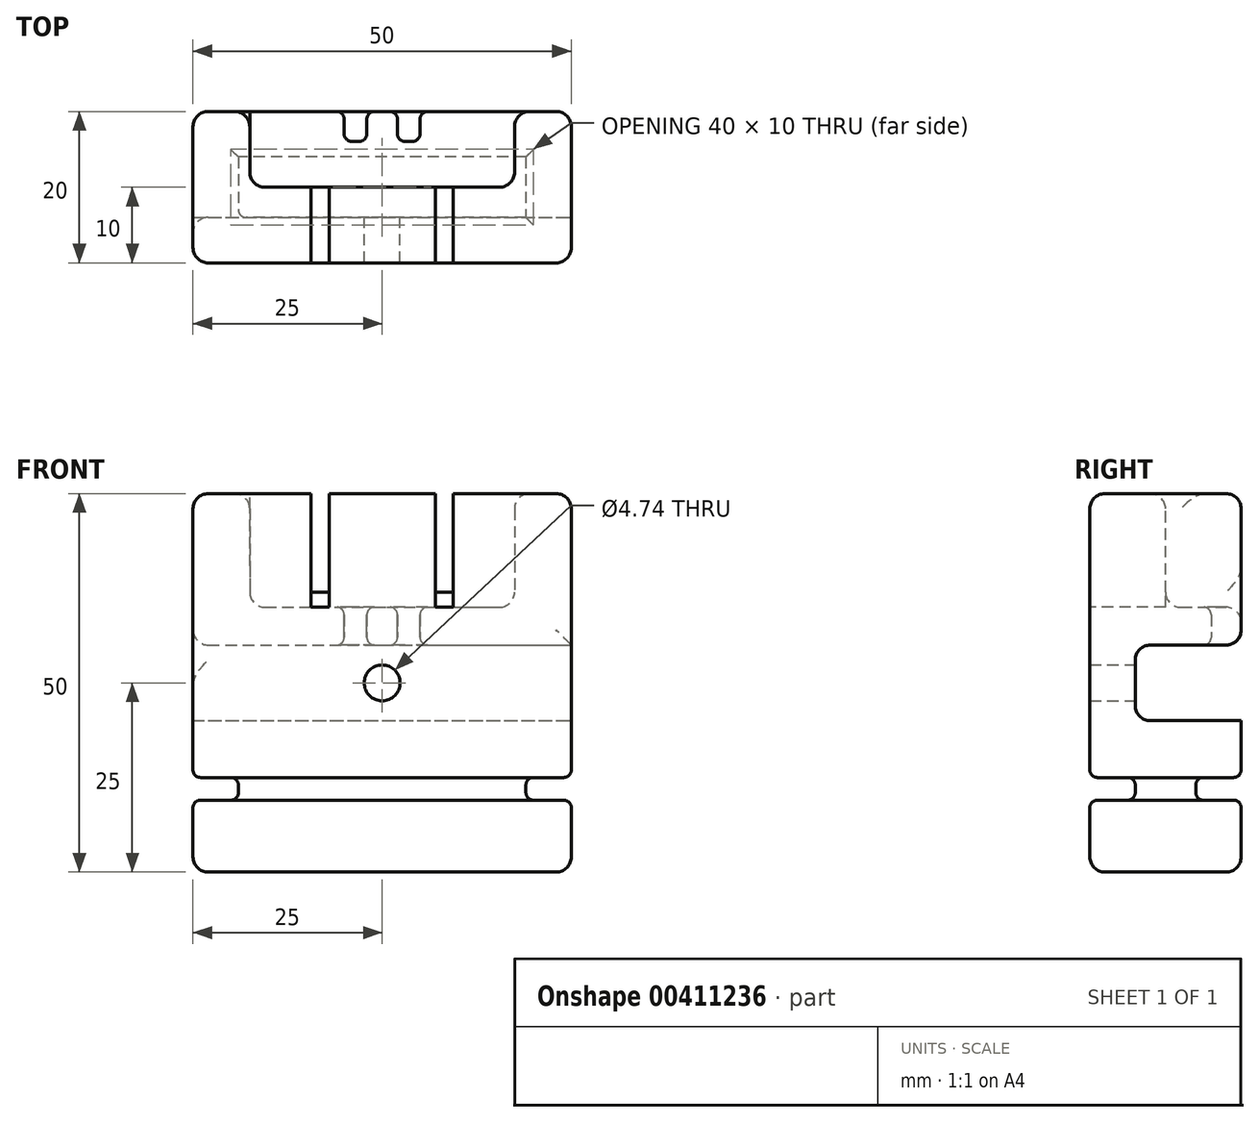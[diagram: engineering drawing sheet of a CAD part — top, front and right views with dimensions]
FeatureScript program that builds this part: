
annotation { "Feature Type Name" : "Feature", "Feature Type Description" : "" }
export const myFeature = defineFeature(function(context is Context, id is Id, definition is map)
    precondition{}
    {
        {
            var Q0;
            Q0=qCreatedBy(makeId("Front.planeOp"),FACE);
            var sketch = newSketch(context, id + "F0", { "sketchPlane" : qUnion([Q0])});
            skLineSegment(sketch, "E0.bottom", {"start": v(-25, 25) * mm, "end": v(25, 25) * mm});
            skLineSegment(sketch, "E0.top", {"start": v(-25, -25) * mm, "end": v(25, -25) * mm});
            skLineSegment(sketch, "E0.left", {"start": v(-25, 25) * mm, "end": v(-25, -25) * mm});
            skLineSegment(sketch, "E0.right", {"start": v(25, 25) * mm, "end": v(25, -25) * mm});
            skSolve(sketch);
        }
        {
            var Q0;
            Q0=makeQuery(id+"F0.imprint","IMPRINT",FACE,{"disambiguationData":[TD([[makeQuery(id+"F0.imprint","IMPRINT",EDGE,{"derivedFrom":sQuery(id+"F0.wireOp",EDGE,"E0.bottom")}),-1.0]])]});
            extrude(context, id + "F1", {"entities" : qUnion([Q0]), "endBound" : BoundingType.SYMMETRIC, "depth" : 20 * mm});
        }
        {
            var Q0;
            Q0=makeQuery(id+"F1.opExtrude","SWEPT_FACE",FACE,{"disambiguationData":[OSD([sQuery(id+"F0.wireOp",EDGE,"E0.right")])]});
            var sketch = newSketch(context, id + "F2", { "sketchPlane" : qUnion([Q0])});
            skLineSegment(sketch, "E1.bottom", {"start": v(-4, 5) * mm, "end": v(10, 5) * mm});
            skLineSegment(sketch, "E1.top", {"start": v(-4, -5) * mm, "end": v(10, -5) * mm});
            skLineSegment(sketch, "E1.left", {"start": v(-4, 5) * mm, "end": v(-4, -5) * mm});
            skLineSegment(sketch, "E1.right", {"start": v(10, 5) * mm, "end": v(10, -5) * mm});
            skSolve(sketch);
        }
        {
            var Q0;
            Q0=makeQuery(id+"F2.imprint","IMPRINT",FACE,{"disambiguationData":[TD([[makeQuery(id+"F2.imprint","IMPRINT",EDGE,{"derivedFrom":sQuery(id+"F2.wireOp",EDGE,"E1.bottom")}),-1.0]])]});
            extrude(context, id + "F3", {"entities" : qUnion([Q0]), "operationType" : NewBodyOperationType.REMOVE, "oppositeDirection" : true, "depth" : 76.7 * mm});
        }
        {
            var Q0;
            Q0=makeQuery(id+"F1.opExtrude","CAP_EDGE",EDGE,{"disambiguationData":[OSD([sQuery(id+"F0.wireOp",EDGE,"E0.bottom")])],"isStart":true});
            var Q1;
            Q1=makeQuery(id+"F3.boolean.opBoolean","COPY",EDGE,{"derivedFrom":makeQuery(id+"F3.opExtrude","SWEPT_EDGE",EDGE,{"disambiguationData":[OSD([sQuery(id+"F2.wireOp",EDGE,"E1.top"),sQuery(id+"F2.wireOp",EDGE,"E1.left")])]})});
            var Q2;
            Q2=makeQuery(id+"F3.boolean.opBoolean","COPY",EDGE,{"derivedFrom":makeQuery(id+"F3.opExtrude","SWEPT_EDGE",EDGE,{"disambiguationData":[OSD([sQuery(id+"F2.wireOp",EDGE,"E1.bottom"),sQuery(id+"F2.wireOp",EDGE,"E1.left")])]})});
            var Q3;
            Q3=makeQuery(id+"F1.opExtrude","CAP_EDGE",EDGE,{"disambiguationData":[OSD([sQuery(id+"F0.wireOp",EDGE,"E0.bottom")])],"isStart":false});
            var Q4;
            Q4=makeQuery(id+"F3.boolean.opBoolean","COPY",EDGE,{"derivedFrom":makeQuery(id+"F3.opExtrude","SWEPT_EDGE",EDGE,{"disambiguationData":[OSD([sQuery(id+"F0.wireOp",EDGE,"E0.right"),sQuery(id+"F2.wireOp",EDGE,"E1.top"),sQuery(id+"F2.wireOp",EDGE,"E1.right")])]})});
            var Q5;
            Q5=makeQuery(id+"F1.opExtrude","CAP_EDGE",EDGE,{"disambiguationData":[OSD([sQuery(id+"F0.wireOp",EDGE,"E0.top")])],"isStart":true});
            var Q6;
            Q6=makeQuery(id+"F1.opExtrude","CAP_EDGE",EDGE,{"disambiguationData":[OSD([sQuery(id+"F0.wireOp",EDGE,"E0.top")])],"isStart":false});
            var Q7;
            Q7=makeQuery(id+"F1.opExtrude","CAP_EDGE",EDGE,{"disambiguationData":[OSD([sQuery(id+"F0.wireOp",EDGE,"E0.right")])],"isStart":false});
            var Q8;
            {var subQ0=sQuery(id+"F0.wireOp",EDGE,"E0.right");var subQ1=sQuery(id+"F0.wireOp",EDGE,"E0.top");Q8=makeQuery(id+"F3.boolean.opBoolean","SPLIT",EDGE,{"disambiguationData":[TD([makeQuery(id+"F1.opExtrude","SWEPT_FACE",FACE,{"disambiguationData":[OSD([subQ1])]})])],"derivedFrom":makeQuery(id+"F1.opExtrude","CAP_EDGE",EDGE,{"disambiguationData":[OSD([subQ0])],"isStart":true})});}
            var Q9;
            {var subQ0=sQuery(id+"F0.wireOp",EDGE,"E0.left");var subQ1=sQuery(id+"F0.wireOp",EDGE,"E0.top");Q9=makeQuery(id+"F3.boolean.opBoolean","SPLIT",EDGE,{"disambiguationData":[TD([makeQuery(id+"F1.opExtrude","SWEPT_FACE",FACE,{"disambiguationData":[OSD([subQ1])]})])],"derivedFrom":makeQuery(id+"F1.opExtrude","CAP_EDGE",EDGE,{"disambiguationData":[OSD([subQ0])],"isStart":true})});}
            var Q10;
            Q10=makeQuery(id+"F1.opExtrude","CAP_EDGE",EDGE,{"disambiguationData":[OSD([sQuery(id+"F0.wireOp",EDGE,"E0.left")])],"isStart":false});
            var Q11;
            {var subQ0=sQuery(id+"F0.wireOp",EDGE,"E0.bottom");var subQ1=sQuery(id+"F0.wireOp",EDGE,"E0.left");Q11=makeQuery(id+"F3.boolean.opBoolean","SPLIT",EDGE,{"disambiguationData":[TD([makeQuery(id+"F1.opExtrude","SWEPT_FACE",FACE,{"disambiguationData":[OSD([subQ0])]})])],"derivedFrom":makeQuery(id+"F1.opExtrude","CAP_EDGE",EDGE,{"disambiguationData":[OSD([subQ1])],"isStart":true})});}
            var Q12;
            Q12=makeQuery(id+"F1.opExtrude","SWEPT_EDGE",EDGE,{"disambiguationData":[OSD([sQuery(id+"F0.wireOp",EDGE,"E0.bottom"),sQuery(id+"F0.wireOp",EDGE,"E0.left")])]});
            var Q13;
            Q13=makeQuery(id+"F1.opExtrude","SWEPT_EDGE",EDGE,{"disambiguationData":[OSD([sQuery(id+"F0.wireOp",EDGE,"E0.bottom"),sQuery(id+"F0.wireOp",EDGE,"E0.right")])]});
            var Q14;
            {var subQ0=sQuery(id+"F0.wireOp",EDGE,"E0.bottom");var subQ1=sQuery(id+"F0.wireOp",EDGE,"E0.right");Q14=makeQuery(id+"F3.boolean.opBoolean","SPLIT",EDGE,{"disambiguationData":[TD([makeQuery(id+"F1.opExtrude","SWEPT_FACE",FACE,{"disambiguationData":[OSD([subQ0])]})])],"derivedFrom":makeQuery(id+"F1.opExtrude","CAP_EDGE",EDGE,{"disambiguationData":[OSD([subQ1])],"isStart":true})});}
            var Q15;
            Q15=makeQuery(id+"F3.boolean.opBoolean","COPY",EDGE,{"derivedFrom":makeQuery(id+"F3.opExtrude","CAP_EDGE",EDGE,{"disambiguationData":[OSD([sQuery(id+"F2.wireOp",EDGE,"E1.top")])],"isStart":true})});
            var Q16;
            Q16=makeQuery(id+"F3.boolean.opBoolean","COPY",EDGE,{"derivedFrom":makeQuery(id+"F3.opExtrude","SWEPT_EDGE",EDGE,{"disambiguationData":[OSD([sQuery(id+"F0.wireOp",EDGE,"E0.right"),sQuery(id+"F2.wireOp",EDGE,"E1.bottom"),sQuery(id+"F2.wireOp",EDGE,"E1.right")])]})});
            var Q17;
            Q17=makeQuery(id+"F3.boolean.opBoolean","INTERSECT",EDGE,{"derivedFrom":[makeQuery(id+"F1.opExtrude","SWEPT_FACE",FACE,{"disambiguationData":[OSD([sQuery(id+"F0.wireOp",EDGE,"E0.left")])]}),makeQuery(id+"F3.opExtrude","SWEPT_FACE",FACE,{"disambiguationData":[OSD([sQuery(id+"F2.wireOp",EDGE,"E1.bottom")])]})]});
            var Q18;
            Q18=makeQuery(id+"F1.opExtrude","SWEPT_EDGE",EDGE,{"disambiguationData":[OSD([sQuery(id+"F0.wireOp",EDGE,"E0.top"),sQuery(id+"F0.wireOp",EDGE,"E0.left")])]});
            var Q19;
            Q19=makeQuery(id+"F1.opExtrude","SWEPT_EDGE",EDGE,{"disambiguationData":[OSD([sQuery(id+"F0.wireOp",EDGE,"E0.top"),sQuery(id+"F0.wireOp",EDGE,"E0.right")])]});
            fillet(context, id + "F4", {"entities" : qUnion([Q0, Q1, Q2, Q3, Q4, Q5, Q6, Q7, Q8, Q9, Q10, Q11, Q12, Q13, Q14, Q15, Q16, Q17, Q18, Q19]), "radius" : 2 * mm, "tangentPropagation" : true, "allowEdgeOverflow" : false});
        }
        {
            var Q0;
            Q0=qCreatedBy(makeId("Right.planeOp"),FACE);
            var sketch = newSketch(context, id + "F5", { "sketchPlane" : qUnion([Q0])});
            skLineSegment(sketch, "E2.bottom", {"start": v(0, 30) * mm, "end": v(13.71, 30) * mm});
            skLineSegment(sketch, "E2.top", {"start": v(0, 10) * mm, "end": v(13.71, 10) * mm});
            skLineSegment(sketch, "E2.left", {"start": v(0, 30) * mm, "end": v(0, 10) * mm});
            skLineSegment(sketch, "E2.right", {"start": v(13.71, 30) * mm, "end": v(13.71, 10) * mm});
            skSolve(sketch);
        }
        {
            var Q0;
            Q0=makeQuery(id+"F5.imprint","IMPRINT",FACE,{"disambiguationData":[TD([[makeQuery(id+"F5.imprint","IMPRINT",EDGE,{"derivedFrom":sQuery(id+"F5.wireOp",EDGE,"E2.bottom")}),-1.0]])]});
            extrude(context, id + "F6", {"entities" : qUnion([Q0]), "operationType" : NewBodyOperationType.REMOVE, "endBound" : BoundingType.SYMMETRIC, "oppositeDirection" : true, "depth" : 35 * mm});
        }
        {
            var Q0;
            Q0=makeQuery(id+"F6.boolean.opBoolean","COPY",EDGE,{"derivedFrom":makeQuery(id+"F6.opExtrude","SWEPT_EDGE",EDGE,{"disambiguationData":[OSD([sQuery(id+"F5.wireOp",EDGE,"E2.top"),sQuery(id+"F5.wireOp",EDGE,"E2.left")])]})});
            var Q1;
            Q1=makeQuery(id+"F6.boolean.opBoolean","INTERSECT",EDGE,{"derivedFrom":[makeQuery(id+"F1.opExtrude","SWEPT_FACE",FACE,{"disambiguationData":[OSD([sQuery(id+"F0.wireOp",EDGE,"E0.bottom")])]}),makeQuery(id+"F6.opExtrude","SWEPT_FACE",FACE,{"disambiguationData":[OSD([sQuery(id+"F5.wireOp",EDGE,"E2.left")])]})]});
            var Q2;
            Q2=makeQuery(id+"F6.boolean.opBoolean","INTERSECT",EDGE,{"derivedFrom":[makeQuery(id+"F1.opExtrude","SWEPT_FACE",FACE,{"disambiguationData":[OSD([sQuery(id+"F0.wireOp",EDGE,"E0.bottom")])]}),makeQuery(id+"F6.opExtrude","CAP_FACE",FACE,{"disambiguationData":[OSD([sQuery(id+"F5.wireOp",EDGE,"E2.bottom"),sQuery(id+"F5.wireOp",EDGE,"E2.top"),sQuery(id+"F5.wireOp",EDGE,"E2.left"),sQuery(id+"F5.wireOp",EDGE,"E2.right")])],"isStart":true})]});
            var Q3;
            Q3=makeQuery(id+"F6.boolean.opBoolean","COPY",EDGE,{"derivedFrom":makeQuery(id+"F6.opExtrude","CAP_EDGE",EDGE,{"disambiguationData":[OSD([sQuery(id+"F5.wireOp",EDGE,"E2.top")])],"isStart":true})});
            var Q4;
            {var subQ0=sQuery(id+"F0.wireOp",EDGE,"E0.bottom");var subQ1=sQuery(id+"F0.wireOp",EDGE,"E0.left");var subQ2=sQuery(id+"F0.wireOp",EDGE,"E0.right");Q4=makeQuery(id+"F6.boolean.opBoolean","INTERSECT",EDGE,{"derivedFrom":[makeQuery(id+"F3.boolean.opBoolean","SPLIT",FACE,{"disambiguationData":[TD([makeQuery(id+"F1.opExtrude","SWEPT_FACE",FACE,{"disambiguationData":[OSD([subQ0])]})])],"derivedFrom":makeQuery(id+"F1.opExtrude","CAP_FACE",FACE,{"disambiguationData":[OSD([subQ0,sQuery(id+"F0.wireOp",EDGE,"E0.top"),subQ1,subQ2])],"isStart":true})}),makeQuery(id+"F6.opExtrude","SWEPT_FACE",FACE,{"disambiguationData":[OSD([sQuery(id+"F5.wireOp",EDGE,"E2.top")])]})]});}
            var Q5;
            Q5=makeQuery(id+"F6.boolean.opBoolean","COPY",EDGE,{"derivedFrom":makeQuery(id+"F6.opExtrude","CAP_EDGE",EDGE,{"disambiguationData":[OSD([sQuery(id+"F5.wireOp",EDGE,"E2.top")])],"isStart":false})});
            var Q6;
            Q6=makeQuery(id+"F6.boolean.opBoolean","COPY",EDGE,{"derivedFrom":makeQuery(id+"F6.opExtrude","CAP_EDGE",EDGE,{"disambiguationData":[OSD([sQuery(id+"F5.wireOp",EDGE,"E2.left")])],"isStart":false})});
            var Q7;
            Q7=makeQuery(id+"F6.boolean.opBoolean","COPY",EDGE,{"derivedFrom":makeQuery(id+"F6.opExtrude","CAP_EDGE",EDGE,{"disambiguationData":[OSD([sQuery(id+"F5.wireOp",EDGE,"E2.left")])],"isStart":true})});
            fillet(context, id + "F7", {"entities" : qUnion([Q0, Q1, Q2, Q3, Q4, Q5, Q6, Q7]), "radius" : 2 * mm, "tangentPropagation" : true, "allowEdgeOverflow" : false});
        }
        {
            var Q0;
            Q0=qCreatedBy(makeId("Top.planeOp"),FACE);
            var sketch = newSketch(context, id + "F8", { "sketchPlane" : qUnion([Q0])});
            skLineSegment(sketch, "E3.bottom", {"start": v(2.01, 11.8) * mm, "end": v(5.01, 11.8) * mm});
            skLineSegment(sketch, "E3.top", {"start": v(2.01, 6.04) * mm, "end": v(5.01, 6.04) * mm});
            skLineSegment(sketch, "E3.left", {"start": v(2.01, 11.8) * mm, "end": v(2.01, 6.04) * mm});
            skLineSegment(sketch, "E3.right", {"start": v(5.01, 11.8) * mm, "end": v(5.01, 6.04) * mm});
            skLineSegment(sketch, "E4.MirrorCS", {"start": v(-2.01, 6.04) * mm, "end": v(-5.01, 6.04) * mm});
            skLineSegment(sketch, "E5.MirrorCS", {"start": v(-5.01, 11.8) * mm, "end": v(-5.01, 6.04) * mm});
            skLineSegment(sketch, "E6.MirrorCS", {"start": v(-2.01, 11.8) * mm, "end": v(-5.01, 11.8) * mm});
            skLineSegment(sketch, "E7.MirrorCS", {"start": v(-2.01, 11.8) * mm, "end": v(-2.01, 6.04) * mm});
            skSolve(sketch);
        }
        {
            var Q0;
            Q0=makeQuery(id+"F8.imprint","IMPRINT",FACE,{"disambiguationData":[TD([[makeQuery(id+"F8.imprint","IMPRINT",EDGE,{"derivedFrom":sQuery(id+"F8.wireOp",EDGE,"E3.bottom")}),-1.0]])]});
            var Q1;
            Q1=makeQuery(id+"F8.imprint","IMPRINT",FACE,{"disambiguationData":[TD([[makeQuery(id+"F8.imprint","IMPRINT",EDGE,{"derivedFrom":sQuery(id+"F8.wireOp",EDGE,"E4.MirrorCS")}),-1.0]])]});
            extrude(context, id + "F9", {"entities" : qUnion([Q0, Q1]), "operationType" : NewBodyOperationType.REMOVE, "depth" : 29.72 * mm});
        }
        {
            var Q0;
            Q0=makeQuery(id+"F9.boolean.opBoolean","INTERSECT",EDGE,{"derivedFrom":[makeQuery(id+"F6.boolean.opBoolean","COPY",FACE,{"derivedFrom":makeQuery(id+"F6.opExtrude","SWEPT_FACE",FACE,{"disambiguationData":[OSD([sQuery(id+"F5.wireOp",EDGE,"E2.top")])]})}),makeQuery(id+"F9.opExtrude","SWEPT_FACE",FACE,{"disambiguationData":[OSD([sQuery(id+"F8.wireOp",EDGE,"E3.top")])]})]});
            var Q1;
            Q1=makeQuery(id+"F9.boolean.opBoolean","COPY",EDGE,{"derivedFrom":makeQuery(id+"F9.opExtrude","SWEPT_EDGE",EDGE,{"disambiguationData":[OSD([sQuery(id+"F8.wireOp",EDGE,"E3.top"),sQuery(id+"F8.wireOp",EDGE,"E3.left")])]})});
            var Q2;
            Q2=makeQuery(id+"F9.boolean.opBoolean","INTERSECT",EDGE,{"derivedFrom":[makeQuery(id+"F6.boolean.opBoolean","COPY",FACE,{"derivedFrom":makeQuery(id+"F6.opExtrude","SWEPT_FACE",FACE,{"disambiguationData":[OSD([sQuery(id+"F5.wireOp",EDGE,"E2.top")])]})}),makeQuery(id+"F9.opExtrude","SWEPT_FACE",FACE,{"disambiguationData":[OSD([sQuery(id+"F8.wireOp",EDGE,"E3.left")])]})]});
            var Q3;
            Q3=makeQuery(id+"F9.boolean.opBoolean","INTERSECT",EDGE,{"derivedFrom":[makeQuery(id+"F6.boolean.opBoolean","COPY",FACE,{"derivedFrom":makeQuery(id+"F6.opExtrude","SWEPT_FACE",FACE,{"disambiguationData":[OSD([sQuery(id+"F5.wireOp",EDGE,"E2.top")])]})}),makeQuery(id+"F9.opExtrude","SWEPT_FACE",FACE,{"disambiguationData":[OSD([sQuery(id+"F8.wireOp",EDGE,"E4.MirrorCS")])]})]});
            var Q4;
            Q4=makeQuery(id+"F9.boolean.opBoolean","INTERSECT",EDGE,{"derivedFrom":[makeQuery(id+"F6.boolean.opBoolean","COPY",FACE,{"derivedFrom":makeQuery(id+"F6.opExtrude","SWEPT_FACE",FACE,{"disambiguationData":[OSD([sQuery(id+"F5.wireOp",EDGE,"E2.top")])]})}),makeQuery(id+"F9.opExtrude","SWEPT_FACE",FACE,{"disambiguationData":[OSD([sQuery(id+"F8.wireOp",EDGE,"E5.MirrorCS")])]})]});
            var Q5;
            Q5=makeQuery(id+"F9.boolean.opBoolean","INTERSECT",EDGE,{"derivedFrom":[makeQuery(id+"F3.boolean.opBoolean","COPY",FACE,{"derivedFrom":makeQuery(id+"F3.opExtrude","SWEPT_FACE",FACE,{"disambiguationData":[OSD([sQuery(id+"F2.wireOp",EDGE,"E1.bottom")])]})}),makeQuery(id+"F9.opExtrude","SWEPT_FACE",FACE,{"disambiguationData":[OSD([sQuery(id+"F8.wireOp",EDGE,"E3.top")])]})]});
            var Q6;
            Q6=makeQuery(id+"F9.boolean.opBoolean","COPY",EDGE,{"derivedFrom":makeQuery(id+"F9.opExtrude","SWEPT_EDGE",EDGE,{"disambiguationData":[OSD([sQuery(id+"F8.wireOp",EDGE,"E3.top"),sQuery(id+"F8.wireOp",EDGE,"E3.right")])]})});
            var Q7;
            {var subQ0=sQuery(id+"F2.wireOp",EDGE,"E1.right");var subQ1=sQuery(id+"F2.wireOp",EDGE,"E1.bottom");var subQ2=sQuery(id+"F0.wireOp",EDGE,"E0.right");Q7=makeQuery(id+"F9.boolean.opBoolean","INTERSECT",EDGE,{"derivedFrom":[makeQuery(id+"F4.opFillet","BLEND_FACE",FACE,{"disambiguationData":[OSD([subQ2,subQ1,subQ0]),TDD([makeQuery(id+"F3.boolean.opBoolean","COPY",EDGE,{"derivedFrom":makeQuery(id+"F3.opExtrude","SWEPT_EDGE",EDGE,{"disambiguationData":[OSD([subQ2,subQ1,subQ0])]})})])]}),makeQuery(id+"F9.opExtrude","SWEPT_FACE",FACE,{"disambiguationData":[OSD([sQuery(id+"F8.wireOp",EDGE,"E3.right")])]})]});}
            var Q8;
            Q8=makeQuery(id+"F9.boolean.opBoolean","INTERSECT",EDGE,{"derivedFrom":[makeQuery(id+"F3.boolean.opBoolean","COPY",FACE,{"derivedFrom":makeQuery(id+"F3.opExtrude","SWEPT_FACE",FACE,{"disambiguationData":[OSD([sQuery(id+"F2.wireOp",EDGE,"E1.bottom")])]})}),makeQuery(id+"F9.opExtrude","SWEPT_FACE",FACE,{"disambiguationData":[OSD([sQuery(id+"F8.wireOp",EDGE,"E7.MirrorCS")])]})]});
            var Q9;
            Q9=makeQuery(id+"F9.boolean.opBoolean","INTERSECT",EDGE,{"derivedFrom":[makeQuery(id+"F3.boolean.opBoolean","COPY",FACE,{"derivedFrom":makeQuery(id+"F3.opExtrude","SWEPT_FACE",FACE,{"disambiguationData":[OSD([sQuery(id+"F2.wireOp",EDGE,"E1.bottom")])]})}),makeQuery(id+"F9.opExtrude","SWEPT_FACE",FACE,{"disambiguationData":[OSD([sQuery(id+"F8.wireOp",EDGE,"E4.MirrorCS")])]})]});
            var Q10;
            Q10=makeQuery(id+"F9.boolean.opBoolean","COPY",EDGE,{"derivedFrom":makeQuery(id+"F9.opExtrude","SWEPT_EDGE",EDGE,{"disambiguationData":[OSD([sQuery(id+"F8.wireOp",EDGE,"E4.MirrorCS"),sQuery(id+"F8.wireOp",EDGE,"E7.MirrorCS")])]})});
            var Q11;
            Q11=makeQuery(id+"F9.boolean.opBoolean","COPY",EDGE,{"derivedFrom":makeQuery(id+"F9.opExtrude","SWEPT_EDGE",EDGE,{"disambiguationData":[OSD([sQuery(id+"F8.wireOp",EDGE,"E4.MirrorCS"),sQuery(id+"F8.wireOp",EDGE,"E5.MirrorCS")])]})});
            fillet(context, id + "F10", {"entities" : qUnion([Q0, Q1, Q2, Q3, Q4, Q5, Q6, Q7, Q8, Q9, Q10, Q11]), "radius" : 1 * mm, "tangentPropagation" : true, "allowEdgeOverflow" : false});
        }
        {
            var Q0;
            {var subQ0=sQuery(id+"F0.wireOp",EDGE,"E0.top");var subQ1=sQuery(id+"F0.wireOp",EDGE,"E0.left");var subQ2=sQuery(id+"F0.wireOp",EDGE,"E0.right");Q0=makeQuery(id+"F3.boolean.opBoolean","SPLIT",FACE,{"disambiguationData":[TD([makeQuery(id+"F1.opExtrude","SWEPT_FACE",FACE,{"disambiguationData":[OSD([subQ0])]})])],"derivedFrom":makeQuery(id+"F1.opExtrude","CAP_FACE",FACE,{"disambiguationData":[OSD([sQuery(id+"F0.wireOp",EDGE,"E0.bottom"),subQ0,subQ1,subQ2])],"isStart":true})});}
            var sketch = newSketch(context, id + "F11", { "sketchPlane" : qUnion([Q0])});
            skLineSegment(sketch, "E8.bottom", {"start": v(-25, -12.5) * mm, "end": v(25, -12.5) * mm});
            skLineSegment(sketch, "E8.top", {"start": v(-25, -15.5) * mm, "end": v(25, -15.5) * mm});
            skLineSegment(sketch, "E8.left", {"start": v(-25, -12.5) * mm, "end": v(-25, -15.5) * mm});
            skLineSegment(sketch, "E8.right", {"start": v(25, -12.5) * mm, "end": v(25, -15.5) * mm});
            skSolve(sketch);
        }
        {
            var Q0;
            {var subQ0=sQuery(id+"F11.wireOp",EDGE,"E8.bottom");var subQ1=sQuery(id+"F0.wireOp",EDGE,"E0.top");var subQ2=makeQuery(id+"F1.opExtrude","SWEPT_FACE",FACE,{"disambiguationData":[OSD([subQ1])]});var subQ3=sQuery(id+"F0.wireOp",EDGE,"E0.left");var subQ5=sQuery(id+"F0.wireOp",EDGE,"E0.right");var subQ8=makeQuery(id+"F1.opExtrude","CAP_FACE",FACE,{"disambiguationData":[OSD([sQuery(id+"F0.wireOp",EDGE,"E0.bottom"),subQ1,subQ3,subQ5])],"isStart":true});var subQ9=makeQuery(id+"F3.boolean.opBoolean","SPLIT",FACE,{"disambiguationData":[TD([subQ2])],"derivedFrom":subQ8});var subQ10=makeQuery(id+"F4.opFillet","BLEND_EDGE",EDGE,{"blendedFrom":[makeQuery(id+"F3.boolean.opBoolean","SPLIT",EDGE,{"disambiguationData":[TD([subQ2])],"derivedFrom":makeQuery(id+"F1.opExtrude","CAP_EDGE",EDGE,{"disambiguationData":[OSD([subQ5])],"isStart":true})}),subQ9],"blendedInto":[subQ9]});var subQ11=makeQuery(id+"F11.imprint","INTERSECT",VERTEX,{"derivedFrom":[subQ10,subQ0]});Q0=makeQuery(id+"F11.imprint","IMPRINT",FACE,{"disambiguationData":[TD([[makeQuery(id+"F11.imprint","IMPRINT",EDGE,{"disambiguationData":[TD([[subQ11,-1.0]])],"derivedFrom":subQ0}),-1.0]])]});}
            var Q1;
            {var subQ0=sQuery(id+"F11.wireOp",EDGE,"E8.left");Q1=makeQuery(id+"F11.imprint","IMPRINT",FACE,{"disambiguationData":[TD([[makeQuery(id+"F11.imprint","IMPRINT",EDGE,{"derivedFrom":subQ0}),1.0]])]});}
            var Q2;
            {var subQ0=sQuery(id+"F11.wireOp",EDGE,"E8.right");Q2=makeQuery(id+"F11.imprint","IMPRINT",FACE,{"disambiguationData":[TD([[makeQuery(id+"F11.imprint","IMPRINT",EDGE,{"derivedFrom":subQ0}),-1.0]])]});}
            extrude(context, id + "F12", {"entities" : qUnion([Q0, Q1, Q2]), "operationType" : NewBodyOperationType.REMOVE, "oppositeDirection" : true, "depth" : 6 * mm});
        }
        {
            var Q0;
            Q0=makeQuery(id+"F1.opExtrude","SWEPT_FACE",FACE,{"disambiguationData":[OSD([sQuery(id+"F0.wireOp",EDGE,"E0.right")])]});
            var sketch = newSketch(context, id + "F13", { "sketchPlane" : qUnion([Q0])});
            skLineSegment(sketch, "E9.bottom", {"start": v(4, -15.5) * mm, "end": v(-15.57, -15.5) * mm});
            skLineSegment(sketch, "E9.top", {"start": v(4, -12.5) * mm, "end": v(-15.57, -12.5) * mm});
            skLineSegment(sketch, "E9.left", {"start": v(4, -15.5) * mm, "end": v(4, -12.5) * mm});
            skLineSegment(sketch, "E9.right", {"start": v(-15.57, -15.5) * mm, "end": v(-15.57, -12.5) * mm});
            skSolve(sketch);
        }
        {
            var Q0;
            {var subQ0=sQuery(id+"F13.wireOp",EDGE,"E9.right");Q0=makeQuery(id+"F13.imprint","IMPRINT",FACE,{"disambiguationData":[TD([[makeQuery(id+"F13.imprint","IMPRINT",EDGE,{"derivedFrom":subQ0}),-1.0]])]});}
            var Q1;
            {var subQ0=sQuery(id+"F13.wireOp",EDGE,"E9.left");Q1=makeQuery(id+"F13.imprint","IMPRINT",FACE,{"disambiguationData":[TD([[makeQuery(id+"F13.imprint","IMPRINT",EDGE,{"derivedFrom":subQ0}),-1.0]])]});}
            extrude(context, id + "F14", {"entities" : qUnion([Q0, Q1]), "operationType" : NewBodyOperationType.REMOVE, "oppositeDirection" : true, "depth" : 6 * mm});
        }
        {
            var Q0;
            Q0=makeQuery(id+"F1.opExtrude","CAP_FACE",FACE,{"disambiguationData":[OSD([sQuery(id+"F0.wireOp",EDGE,"E0.bottom"),sQuery(id+"F0.wireOp",EDGE,"E0.top"),sQuery(id+"F0.wireOp",EDGE,"E0.left"),sQuery(id+"F0.wireOp",EDGE,"E0.right")])],"isStart":false});
            var sketch = newSketch(context, id + "F15", { "sketchPlane" : qUnion([Q0])});
            skLineSegment(sketch, "E10.bottom", {"start": v(19, -15.5) * mm, "end": v(-31.6, -15.5) * mm});
            skLineSegment(sketch, "E10.top", {"start": v(19, -12.5) * mm, "end": v(-31.6, -12.5) * mm});
            skLineSegment(sketch, "E10.left", {"start": v(19, -15.5) * mm, "end": v(19, -12.5) * mm});
            skLineSegment(sketch, "E10.right", {"start": v(-31.6, -15.5) * mm, "end": v(-31.6, -12.5) * mm});
            skSolve(sketch);
        }
        {
            var Q0;
            {var subQ0=sQuery(id+"F15.wireOp",EDGE,"E10.right");Q0=makeQuery(id+"F15.imprint","IMPRINT",FACE,{"disambiguationData":[TD([[makeQuery(id+"F15.imprint","IMPRINT",EDGE,{"derivedFrom":subQ0}),-1.0]])]});}
            var Q1;
            {var subQ0=sQuery(id+"F15.wireOp",EDGE,"E10.left");Q1=makeQuery(id+"F15.imprint","IMPRINT",FACE,{"disambiguationData":[TD([[makeQuery(id+"F15.imprint","IMPRINT",EDGE,{"derivedFrom":subQ0}),1.0]])]});}
            extrude(context, id + "F16", {"entities" : qUnion([Q0, Q1]), "operationType" : NewBodyOperationType.REMOVE, "oppositeDirection" : true, "depth" : 6 * mm});
        }
        {
            var Q0;
            Q0=makeQuery(id+"F1.opExtrude","SWEPT_FACE",FACE,{"disambiguationData":[OSD([sQuery(id+"F0.wireOp",EDGE,"E0.left")])]});
            var sketch = newSketch(context, id + "F17", { "sketchPlane" : qUnion([Q0])});
            skLineSegment(sketch, "E11.bottom", {"start": v(-4, -12.5) * mm, "end": v(13.16, -12.5) * mm});
            skLineSegment(sketch, "E11.top", {"start": v(-4, -15.5) * mm, "end": v(13.16, -15.5) * mm});
            skLineSegment(sketch, "E11.left", {"start": v(-4, -12.5) * mm, "end": v(-4, -15.5) * mm});
            skLineSegment(sketch, "E11.right", {"start": v(13.16, -12.5) * mm, "end": v(13.16, -15.5) * mm});
            skSolve(sketch);
        }
        {
            var Q0;
            {var subQ0=sQuery(id+"F17.wireOp",EDGE,"E11.left");Q0=makeQuery(id+"F17.imprint","IMPRINT",FACE,{"disambiguationData":[TD([[makeQuery(id+"F17.imprint","IMPRINT",EDGE,{"derivedFrom":subQ0}),1.0]])]});}
            var Q1;
            {var subQ15=sQuery(id+"F17.wireOp",EDGE,"E11.right");Q1=makeQuery(id+"F17.imprint","IMPRINT",FACE,{"disambiguationData":[TD([[makeQuery(id+"F17.imprint","IMPRINT",EDGE,{"derivedFrom":subQ15}),-1.0]])]});}
            extrude(context, id + "F18", {"entities" : qUnion([Q0, Q1]), "operationType" : NewBodyOperationType.REMOVE, "oppositeDirection" : true, "depth" : 6 * mm});
        }
        {
            var Q0;
            Q0=makeQuery(id+"F12.boolean.opBoolean","COPY",EDGE,{"derivedFrom":makeQuery(id+"F12.opExtrude","CAP_EDGE",EDGE,{"disambiguationData":[OSD([sQuery(id+"F11.wireOp",EDGE,"E8.top")])],"isStart":true})});
            var Q1;
            Q1=makeQuery(id+"F12.boolean.opBoolean","COPY",EDGE,{"derivedFrom":makeQuery(id+"F12.opExtrude","CAP_EDGE",EDGE,{"disambiguationData":[OSD([sQuery(id+"F11.wireOp",EDGE,"E8.top")])],"isStart":false})});
            var Q2;
            Q2=makeQuery(id+"F14.boolean.opBoolean","COPY",EDGE,{"derivedFrom":makeQuery(id+"F14.opExtrude","CAP_EDGE",EDGE,{"disambiguationData":[OSD([sQuery(id+"F13.wireOp",EDGE,"E9.top")])],"isStart":false})});
            var Q3;
            Q3=makeQuery(id+"F12.boolean.opBoolean","COPY",EDGE,{"derivedFrom":makeQuery(id+"F12.opExtrude","CAP_EDGE",EDGE,{"disambiguationData":[OSD([sQuery(id+"F11.wireOp",EDGE,"E8.bottom")])],"isStart":false})});
            var Q4;
            Q4=makeQuery(id+"F12.boolean.opBoolean","COPY",EDGE,{"derivedFrom":makeQuery(id+"F12.opExtrude","CAP_EDGE",EDGE,{"disambiguationData":[OSD([sQuery(id+"F11.wireOp",EDGE,"E8.bottom")])],"isStart":true})});
            var Q5;
            {var subQ0=sQuery(id+"F0.wireOp",EDGE,"E0.right");var subQ1=sQuery(id+"F0.wireOp",EDGE,"E0.top");Q5=makeQuery(id+"F12.boolean.opBoolean","INTERSECT",EDGE,{"derivedFrom":[makeQuery(id+"F4.opFillet","BLEND_FACE",FACE,{"disambiguationData":[OSD([subQ0]),TDD([makeQuery(id+"F3.boolean.opBoolean","SPLIT",EDGE,{"disambiguationData":[TD([makeQuery(id+"F1.opExtrude","SWEPT_FACE",FACE,{"disambiguationData":[OSD([subQ1])]})])],"derivedFrom":makeQuery(id+"F1.opExtrude","CAP_EDGE",EDGE,{"disambiguationData":[OSD([subQ0])],"isStart":true})})])]}),makeQuery(id+"F12.opExtrude","SWEPT_FACE",FACE,{"disambiguationData":[OSD([sQuery(id+"F11.wireOp",EDGE,"E8.bottom")])]})]});}
            var Q6;
            Q6=makeQuery(id+"F14.boolean.opBoolean","MERGE",EDGE,{"derivedFrom":[makeQuery(id+"F12.boolean.opBoolean","COPY",EDGE,{"derivedFrom":makeQuery(id+"F12.opExtrude","SWEPT_EDGE",EDGE,{"disambiguationData":[OSD([sQuery(id+"F11.wireOp",EDGE,"E8.bottom"),sQuery(id+"F11.wireOp",EDGE,"E8.left")])]})}),makeQuery(id+"F14.opExtrude","CAP_EDGE",EDGE,{"disambiguationData":[OSD([sQuery(id+"F13.wireOp",EDGE,"E9.top")])],"isStart":true})]});
            var Q7;
            Q7=makeQuery(id+"F14.boolean.opBoolean","COPY",EDGE,{"derivedFrom":makeQuery(id+"F14.opExtrude","CAP_EDGE",EDGE,{"disambiguationData":[OSD([sQuery(id+"F13.wireOp",EDGE,"E9.left")])],"isStart":false})});
            var Q8;
            Q8=makeQuery(id+"F14.boolean.opBoolean","COPY",EDGE,{"derivedFrom":makeQuery(id+"F14.opExtrude","CAP_EDGE",EDGE,{"disambiguationData":[OSD([sQuery(id+"F13.wireOp",EDGE,"E9.bottom")])],"isStart":false})});
            var Q9;
            Q9=makeQuery(id+"F14.boolean.opBoolean","MERGE",EDGE,{"derivedFrom":[makeQuery(id+"F12.boolean.opBoolean","COPY",EDGE,{"derivedFrom":makeQuery(id+"F12.opExtrude","SWEPT_EDGE",EDGE,{"disambiguationData":[OSD([sQuery(id+"F11.wireOp",EDGE,"E8.top"),sQuery(id+"F11.wireOp",EDGE,"E8.left")])]})}),makeQuery(id+"F14.opExtrude","CAP_EDGE",EDGE,{"disambiguationData":[OSD([sQuery(id+"F13.wireOp",EDGE,"E9.bottom")])],"isStart":true})]});
            var Q10;
            {var subQ0=sQuery(id+"F0.wireOp",EDGE,"E0.right");var subQ1=sQuery(id+"F0.wireOp",EDGE,"E0.top");Q10=makeQuery(id+"F12.boolean.opBoolean","INTERSECT",EDGE,{"derivedFrom":[makeQuery(id+"F4.opFillet","BLEND_FACE",FACE,{"disambiguationData":[OSD([subQ0]),TDD([makeQuery(id+"F3.boolean.opBoolean","SPLIT",EDGE,{"disambiguationData":[TD([makeQuery(id+"F1.opExtrude","SWEPT_FACE",FACE,{"disambiguationData":[OSD([subQ1])]})])],"derivedFrom":makeQuery(id+"F1.opExtrude","CAP_EDGE",EDGE,{"disambiguationData":[OSD([subQ0])],"isStart":true})})])]}),makeQuery(id+"F12.opExtrude","SWEPT_FACE",FACE,{"disambiguationData":[OSD([sQuery(id+"F11.wireOp",EDGE,"E8.top")])]})]});}
            var Q11;
            {var subQ0=sQuery(id+"F0.wireOp",EDGE,"E0.right");Q11=makeQuery(id+"F14.boolean.opBoolean","INTERSECT",EDGE,{"derivedFrom":[makeQuery(id+"F4.opFillet","BLEND_FACE",FACE,{"disambiguationData":[OSD([subQ0]),TDD([makeQuery(id+"F1.opExtrude","CAP_EDGE",EDGE,{"disambiguationData":[OSD([subQ0])],"isStart":false})])]}),makeQuery(id+"F14.opExtrude","SWEPT_FACE",FACE,{"disambiguationData":[OSD([sQuery(id+"F13.wireOp",EDGE,"E9.bottom")])]})]});}
            var Q12;
            Q12=makeQuery(id+"F16.boolean.opBoolean","COPY",EDGE,{"derivedFrom":makeQuery(id+"F16.opExtrude","CAP_EDGE",EDGE,{"disambiguationData":[OSD([sQuery(id+"F15.wireOp",EDGE,"E10.bottom")])],"isStart":false})});
            var Q13;
            Q13=makeQuery(id+"F16.boolean.opBoolean","MERGE",EDGE,{"derivedFrom":[makeQuery(id+"F14.boolean.opBoolean","INTERSECT",EDGE,{"derivedFrom":[makeQuery(id+"F1.opExtrude","CAP_FACE",FACE,{"disambiguationData":[OSD([sQuery(id+"F0.wireOp",EDGE,"E0.bottom"),sQuery(id+"F0.wireOp",EDGE,"E0.top"),sQuery(id+"F0.wireOp",EDGE,"E0.left"),sQuery(id+"F0.wireOp",EDGE,"E0.right")])],"isStart":false}),makeQuery(id+"F14.opExtrude","SWEPT_FACE",FACE,{"disambiguationData":[OSD([sQuery(id+"F13.wireOp",EDGE,"E9.bottom")])]})]}),makeQuery(id+"F16.opExtrude","CAP_EDGE",EDGE,{"disambiguationData":[OSD([sQuery(id+"F15.wireOp",EDGE,"E10.bottom")])],"isStart":true})]});
            var Q14;
            Q14=makeQuery(id+"F16.boolean.opBoolean","COPY",EDGE,{"derivedFrom":makeQuery(id+"F16.opExtrude","CAP_EDGE",EDGE,{"disambiguationData":[OSD([sQuery(id+"F15.wireOp",EDGE,"E10.top")])],"isStart":false})});
            var Q15;
            Q15=makeQuery(id+"F16.boolean.opBoolean","MERGE",EDGE,{"derivedFrom":[makeQuery(id+"F14.boolean.opBoolean","INTERSECT",EDGE,{"derivedFrom":[makeQuery(id+"F1.opExtrude","CAP_FACE",FACE,{"disambiguationData":[OSD([sQuery(id+"F0.wireOp",EDGE,"E0.bottom"),sQuery(id+"F0.wireOp",EDGE,"E0.top"),sQuery(id+"F0.wireOp",EDGE,"E0.left"),sQuery(id+"F0.wireOp",EDGE,"E0.right")])],"isStart":false}),makeQuery(id+"F14.opExtrude","SWEPT_FACE",FACE,{"disambiguationData":[OSD([sQuery(id+"F13.wireOp",EDGE,"E9.top")])]})]}),makeQuery(id+"F16.opExtrude","CAP_EDGE",EDGE,{"disambiguationData":[OSD([sQuery(id+"F15.wireOp",EDGE,"E10.top")])],"isStart":true})]});
            var Q16;
            Q16=makeQuery(id+"F18.boolean.opBoolean","COPY",EDGE,{"derivedFrom":makeQuery(id+"F18.opExtrude","CAP_EDGE",EDGE,{"disambiguationData":[OSD([sQuery(id+"F17.wireOp",EDGE,"E11.bottom")])],"isStart":false})});
            var Q17;
            Q17=makeQuery(id+"F18.boolean.opBoolean","MERGE",EDGE,{"derivedFrom":[makeQuery(id+"F12.boolean.opBoolean","COPY",EDGE,{"derivedFrom":makeQuery(id+"F12.opExtrude","SWEPT_EDGE",EDGE,{"disambiguationData":[OSD([sQuery(id+"F11.wireOp",EDGE,"E8.bottom"),sQuery(id+"F11.wireOp",EDGE,"E8.right")])]})}),makeQuery(id+"F16.boolean.opBoolean","INTERSECT",EDGE,{"derivedFrom":[makeQuery(id+"F1.opExtrude","SWEPT_FACE",FACE,{"disambiguationData":[OSD([sQuery(id+"F0.wireOp",EDGE,"E0.left")])]}),makeQuery(id+"F16.opExtrude","SWEPT_FACE",FACE,{"disambiguationData":[OSD([sQuery(id+"F15.wireOp",EDGE,"E10.top")])]})]}),makeQuery(id+"F18.opExtrude","CAP_EDGE",EDGE,{"disambiguationData":[OSD([sQuery(id+"F17.wireOp",EDGE,"E11.bottom")])],"isStart":true})]});
            var Q18;
            {var subQ0=sQuery(id+"F0.wireOp",EDGE,"E0.left");Q18=makeQuery(id+"F16.boolean.opBoolean","INTERSECT",EDGE,{"derivedFrom":[makeQuery(id+"F4.opFillet","BLEND_FACE",FACE,{"disambiguationData":[OSD([subQ0]),TDD([makeQuery(id+"F1.opExtrude","CAP_EDGE",EDGE,{"disambiguationData":[OSD([subQ0])],"isStart":false})])]}),makeQuery(id+"F16.opExtrude","SWEPT_FACE",FACE,{"disambiguationData":[OSD([sQuery(id+"F15.wireOp",EDGE,"E10.top")])]})]});}
            var Q19;
            Q19=makeQuery(id+"F18.boolean.opBoolean","INTERSECT",EDGE,{"derivedFrom":[makeQuery(id+"F16.boolean.opBoolean","COPY",FACE,{"derivedFrom":makeQuery(id+"F16.opExtrude","CAP_FACE",FACE,{"disambiguationData":[OSD([sQuery(id+"F15.wireOp",EDGE,"E10.bottom"),sQuery(id+"F15.wireOp",EDGE,"E10.top"),sQuery(id+"F15.wireOp",EDGE,"E10.left"),sQuery(id+"F15.wireOp",EDGE,"E10.right")])],"isStart":false})}),makeQuery(id+"F18.opExtrude","CAP_FACE",FACE,{"disambiguationData":[OSD([sQuery(id+"F17.wireOp",EDGE,"E11.bottom"),sQuery(id+"F17.wireOp",EDGE,"E11.top"),sQuery(id+"F17.wireOp",EDGE,"E11.left"),sQuery(id+"F17.wireOp",EDGE,"E11.right")])],"isStart":false})]});
            var Q20;
            Q20=makeQuery(id+"F18.boolean.opBoolean","COPY",EDGE,{"derivedFrom":makeQuery(id+"F18.opExtrude","CAP_EDGE",EDGE,{"disambiguationData":[OSD([sQuery(id+"F17.wireOp",EDGE,"E11.left")])],"isStart":false})});
            var Q21;
            Q21=makeQuery(id+"F18.boolean.opBoolean","COPY",EDGE,{"derivedFrom":makeQuery(id+"F18.opExtrude","CAP_EDGE",EDGE,{"disambiguationData":[OSD([sQuery(id+"F17.wireOp",EDGE,"E11.top")])],"isStart":false})});
            var Q22;
            {var subQ0=sQuery(id+"F0.wireOp",EDGE,"E0.left");var subQ1=sQuery(id+"F0.wireOp",EDGE,"E0.top");Q22=makeQuery(id+"F12.boolean.opBoolean","INTERSECT",EDGE,{"derivedFrom":[makeQuery(id+"F4.opFillet","BLEND_FACE",FACE,{"disambiguationData":[OSD([subQ0]),TDD([makeQuery(id+"F3.boolean.opBoolean","SPLIT",EDGE,{"disambiguationData":[TD([makeQuery(id+"F1.opExtrude","SWEPT_FACE",FACE,{"disambiguationData":[OSD([subQ1])]})])],"derivedFrom":makeQuery(id+"F1.opExtrude","CAP_EDGE",EDGE,{"disambiguationData":[OSD([subQ0])],"isStart":true})})])]}),makeQuery(id+"F12.opExtrude","SWEPT_FACE",FACE,{"disambiguationData":[OSD([sQuery(id+"F11.wireOp",EDGE,"E8.top")])]})]});}
            var Q23;
            Q23=makeQuery(id+"F18.boolean.opBoolean","MERGE",EDGE,{"derivedFrom":[makeQuery(id+"F12.boolean.opBoolean","COPY",EDGE,{"derivedFrom":makeQuery(id+"F12.opExtrude","SWEPT_EDGE",EDGE,{"disambiguationData":[OSD([sQuery(id+"F11.wireOp",EDGE,"E8.top"),sQuery(id+"F11.wireOp",EDGE,"E8.right")])]})}),makeQuery(id+"F16.boolean.opBoolean","INTERSECT",EDGE,{"derivedFrom":[makeQuery(id+"F1.opExtrude","SWEPT_FACE",FACE,{"disambiguationData":[OSD([sQuery(id+"F0.wireOp",EDGE,"E0.left")])]}),makeQuery(id+"F16.opExtrude","SWEPT_FACE",FACE,{"disambiguationData":[OSD([sQuery(id+"F15.wireOp",EDGE,"E10.bottom")])]})]}),makeQuery(id+"F18.opExtrude","CAP_EDGE",EDGE,{"disambiguationData":[OSD([sQuery(id+"F17.wireOp",EDGE,"E11.top")])],"isStart":true})]});
            var Q24;
            {var subQ0=sQuery(id+"F0.wireOp",EDGE,"E0.left");Q24=makeQuery(id+"F16.boolean.opBoolean","INTERSECT",EDGE,{"derivedFrom":[makeQuery(id+"F4.opFillet","BLEND_FACE",FACE,{"disambiguationData":[OSD([subQ0]),TDD([makeQuery(id+"F1.opExtrude","CAP_EDGE",EDGE,{"disambiguationData":[OSD([subQ0])],"isStart":false})])]}),makeQuery(id+"F16.opExtrude","SWEPT_FACE",FACE,{"disambiguationData":[OSD([sQuery(id+"F15.wireOp",EDGE,"E10.bottom")])]})]});}
            var Q25;
            {var subQ0=sQuery(id+"F0.wireOp",EDGE,"E0.left");var subQ1=sQuery(id+"F0.wireOp",EDGE,"E0.top");Q25=makeQuery(id+"F12.boolean.opBoolean","INTERSECT",EDGE,{"derivedFrom":[makeQuery(id+"F4.opFillet","BLEND_FACE",FACE,{"disambiguationData":[OSD([subQ0]),TDD([makeQuery(id+"F3.boolean.opBoolean","SPLIT",EDGE,{"disambiguationData":[TD([makeQuery(id+"F1.opExtrude","SWEPT_FACE",FACE,{"disambiguationData":[OSD([subQ1])]})])],"derivedFrom":makeQuery(id+"F1.opExtrude","CAP_EDGE",EDGE,{"disambiguationData":[OSD([subQ0])],"isStart":true})})])]}),makeQuery(id+"F12.opExtrude","SWEPT_FACE",FACE,{"disambiguationData":[OSD([sQuery(id+"F11.wireOp",EDGE,"E8.bottom")])]})]});}
            var Q26;
            Q26=makeQuery(id+"F16.boolean.opBoolean","COPY",EDGE,{"derivedFrom":makeQuery(id+"F16.opExtrude","CAP_EDGE",EDGE,{"disambiguationData":[OSD([sQuery(id+"F15.wireOp",EDGE,"E10.left")])],"isStart":false})});
            fillet(context, id + "F19", {"entities" : qUnion([Q0, Q1, Q2, Q3, Q4, Q5, Q6, Q7, Q8, Q9, Q10, Q11, Q12, Q13, Q14, Q15, Q16, Q17, Q18, Q19, Q20, Q21, Q22, Q23, Q24, Q25, Q26]), "radius" : 1 * mm, "tangentPropagation" : true, "allowEdgeOverflow" : false});
        }
        {
            var Q0;
            Q0=makeQuery(id+"F3.boolean.opBoolean","COPY",FACE,{"derivedFrom":makeQuery(id+"F3.opExtrude","SWEPT_FACE",FACE,{"disambiguationData":[OSD([sQuery(id+"F2.wireOp",EDGE,"E1.left")])]})});
            var sketch = newSketch(context, id + "F20", { "sketchPlane" : qUnion([Q0])});
            skCircle(sketch, "E12", {"center": v(0, 0) * mm, "radius": 2.37 * mm});
            skSolve(sketch);
        }
        {
            var Q0;
            Q0 = qSketchRegion(id + "F20", true);
            extrude(context, id + "F21", {"entities" : qUnion([Q0]), "operationType" : NewBodyOperationType.REMOVE, "oppositeDirection" : true, "depth" : 25 * mm});
        }
        {
            var Q0;
            Q0=makeQuery(id+"F1.opExtrude","SWEPT_FACE",FACE,{"disambiguationData":[OSD([sQuery(id+"F0.wireOp",EDGE,"E0.bottom")])]});
            cPlane(context, id + "F22", {"entities" : qUnion([Q0]), "cplaneType" : CPlaneType.OFFSET, "offset" : 25 * mm, "width" : 150 * mm, "height" : 150 * mm});
        }
        {
            var Q0;
            Q0=qCreatedBy(id+"F22.planeOp",FACE);
            var sketch = newSketch(context, id + "F23", { "sketchPlane" : qUnion([Q0])});
            skLineSegment(sketch, "E13.bottom", {"start": v(9.4, 0) * mm, "end": v(7.02, 0) * mm});
            skLineSegment(sketch, "E13.top", {"start": v(9.4, -10) * mm, "end": v(7.02, -10) * mm});
            skLineSegment(sketch, "E13.left", {"start": v(9.4, 0) * mm, "end": v(9.4, -10) * mm});
            skLineSegment(sketch, "E13.right", {"start": v(7.02, 0) * mm, "end": v(7.02, -10) * mm});
            skLineSegment(sketch, "E14.MirrorCS", {"start": v(-9.4, 0) * mm, "end": v(-7.02, 0) * mm});
            skLineSegment(sketch, "E15.MirrorCS", {"start": v(-9.4, -10) * mm, "end": v(-7.02, -10) * mm});
            skLineSegment(sketch, "E16.MirrorCS", {"start": v(-9.4, 0) * mm, "end": v(-9.4, -10) * mm});
            skLineSegment(sketch, "E17.MirrorCS", {"start": v(-7.02, 0) * mm, "end": v(-7.02, -10) * mm});
            skSolve(sketch);
        }
        {
            var Q0;
            Q0 = qSketchRegion(id + "F23", true);
            extrude(context, id + "F24", {"entities" : qUnion([Q0]), "operationType" : NewBodyOperationType.REMOVE, "oppositeDirection" : true, "depth" : 40 * mm});
        }
    });
